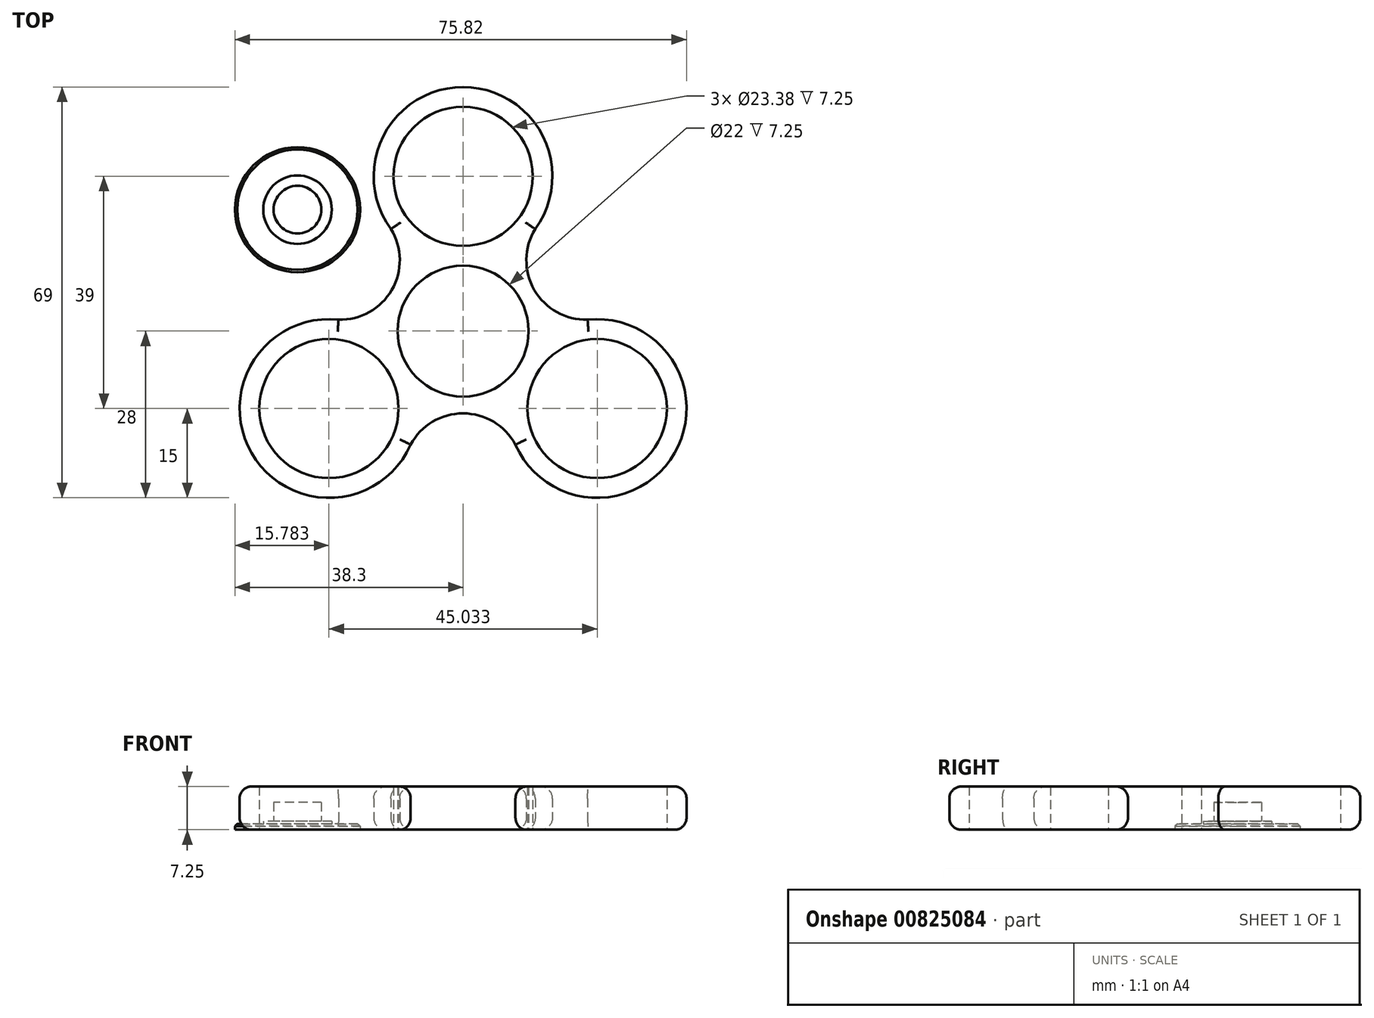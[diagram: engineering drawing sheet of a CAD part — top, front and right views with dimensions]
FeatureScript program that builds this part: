
annotation { "Feature Type Name" : "Feature", "Feature Type Description" : "" }
export const myFeature = defineFeature(function(context is Context, id is Id, definition is map)
    precondition{}
    {
        {
            var Q0;
            Q0=qCreatedBy(makeId("Top.planeOp"),FACE);
            var sketch = newSketch(context, id + "F0", { "sketchPlane" : qUnion([Q0])});
            skCircle(sketch, "E0", {"center": v(0, 26) * mm, "radius": 11.7 * mm});
            skArc(sketch, "E1", {"start": v(12.11, 17.15) * mm, "mid": v(0, 41) * mm, "end": v(-12.11, 17.15) * mm});
            skArc(sketch, "E2.1.0", {"start": v(-20.91, 1.91) * mm, "mid": v(-35.5, -20.5) * mm, "end": v(-8.8, -19.07) * mm});
            skCircle(sketch, "E2.1.2", {"center": v(-22.52, -13) * mm, "radius": 11.7 * mm});
            skArc(sketch, "E2.2.0", {"start": v(8.8, -19.07) * mm, "mid": v(35.5, -20.5) * mm, "end": v(20.91, 1.91) * mm});
            skCircle(sketch, "E2.2.2", {"center": v(22.52, -13) * mm, "radius": 11.7 * mm});
            skPoint(sketch, "E2.center", {"position": v(0, 0) * mm});
            skCircle(sketch, "E3", {"center": v(0, 0) * mm, "radius": 11 * mm});
            skCircle(sketch, "E4", {"center": v(0, 0) * mm, "radius": 21 * mm, "construction": true});
            skArc(sketch, "E5", {"start": v(12.11, 17.15) * mm, "mid": v(11.97, 6.9) * mm, "end": v(20.91, 1.91) * mm});
            skArc(sketch, "E6.1.0", {"start": v(-20.91, 1.91) * mm, "mid": v(-11.97, 6.9) * mm, "end": v(-12.11, 17.15) * mm});
            skArc(sketch, "E6.2.0", {"start": v(8.8, -19.07) * mm, "mid": v(0, -13.82) * mm, "end": v(-8.8, -19.07) * mm});
            skSolve(sketch);
        }
        {
            var Q0;
            Q0=makeQuery(id+"F0.imprint","IMPRINT",FACE,{"disambiguationData":[TD([[makeQuery(id+"F0.imprint","IMPRINT",EDGE,{"derivedFrom":sQuery(id+"F0.wireOp",EDGE,"E0")}),-1.0]])]});
            extrude(context, id + "F1", {"entities" : qUnion([Q0]), "depth" : 7.25 * mm, "offsetDistance" : 25 * mm});
        }
        {
            var Q0;
            Q0=makeQuery(id+"F1.opExtrude","CAP_EDGE",EDGE,{"disambiguationData":[OSD([sQuery(id+"F0.wireOp",EDGE,"E2.1.0")])],"isStart":false});
            var Q1;
            Q1=makeQuery(id+"F1.opExtrude","CAP_EDGE",EDGE,{"disambiguationData":[OSD([sQuery(id+"F0.wireOp",EDGE,"E1")])],"isStart":false});
            var Q2;
            Q2=makeQuery(id+"F1.opExtrude","CAP_EDGE",EDGE,{"disambiguationData":[OSD([sQuery(id+"F0.wireOp",EDGE,"E2.2.0")])],"isStart":false});
            var Q3;
            Q3=makeQuery(id+"F1.opExtrude","CAP_EDGE",EDGE,{"disambiguationData":[OSD([sQuery(id+"F0.wireOp",EDGE,"E2.1.0")])],"isStart":true});
            var Q4;
            Q4=makeQuery(id+"F1.opExtrude","CAP_EDGE",EDGE,{"disambiguationData":[OSD([sQuery(id+"F0.wireOp",EDGE,"E2.2.0")])],"isStart":true});
            var Q5;
            Q5=makeQuery(id+"F1.opExtrude","CAP_EDGE",EDGE,{"disambiguationData":[OSD([sQuery(id+"F0.wireOp",EDGE,"E1")])],"isStart":true});
            fillet(context, id + "F2", {"entities" : qUnion([Q0, Q1, Q2, Q3, Q4, Q5]), "radius" : 2 * mm, "tangentPropagation" : true, "allowEdgeOverflow" : false});
        }
        {
            var Q0;
            Q0=qCreatedBy(makeId("Top.planeOp"),FACE);
            var sketch = newSketch(context, id + "F3", { "sketchPlane" : qUnion([Q0])});
            skCircle(sketch, "E7", {"center": v(-27.8, 20.4) * mm, "radius": 10.5 * mm});
            skCircle(sketch, "E8", {"center": v(-27.8, 20.4) * mm, "radius": 5.75 * mm});
            skCircle(sketch, "E9", {"center": v(-27.8, 20.4) * mm, "radius": 4 * mm});
            skSolve(sketch);
        }
        {
            var Q0;
            Q0=makeQuery(id+"F3.imprint","IMPRINT",FACE,{"disambiguationData":[TD([[makeQuery(id+"F3.imprint","IMPRINT",EDGE,{"derivedFrom":sQuery(id+"F3.wireOp",EDGE,"E8")}),1.0]])]});
            extrude(context, id + "F4", {"entities" : qUnion([Q0]), "operationType" : NewBodyOperationType.ADD, "depth" : 1.4 * mm, "offsetDistance" : 25 * mm});
        }
        {
            var Q0;
            Q0=makeQuery(id+"F3.imprint","IMPRINT",FACE,{"disambiguationData":[TD([[makeQuery(id+"F3.imprint","IMPRINT",EDGE,{"derivedFrom":sQuery(id+"F3.wireOp",EDGE,"E7")}),1.0]])]});
            extrude(context, id + "F5", {"entities" : qUnion([Q0]), "operationType" : NewBodyOperationType.ADD, "depth" : 1 * mm, "offsetDistance" : 25 * mm});
        }
        {
            var Q0;
            Q0=makeQuery(id+"F3.imprint","IMPRINT",FACE,{"disambiguationData":[TD([[makeQuery(id+"F3.imprint","IMPRINT",EDGE,{"derivedFrom":sQuery(id+"F3.wireOp",EDGE,"E9")}),1.0]])]});
            extrude(context, id + "F6", {"entities" : qUnion([Q0]), "operationType" : NewBodyOperationType.ADD, "depth" : 4.6 * mm, "offsetDistance" : 25 * mm});
        }
        {
            var Q0;
            Q0=makeQuery(id+"F5.opExtrude","CAP_EDGE",EDGE,{"disambiguationData":[OSD([sQuery(id+"F3.wireOp",EDGE,"E7")])],"isStart":false});
            chamfer(context, id + "F7", {"entities" : qUnion([Q0]), "width" : .4 * mm, "tangentPropagation" : true});
        }
    });
